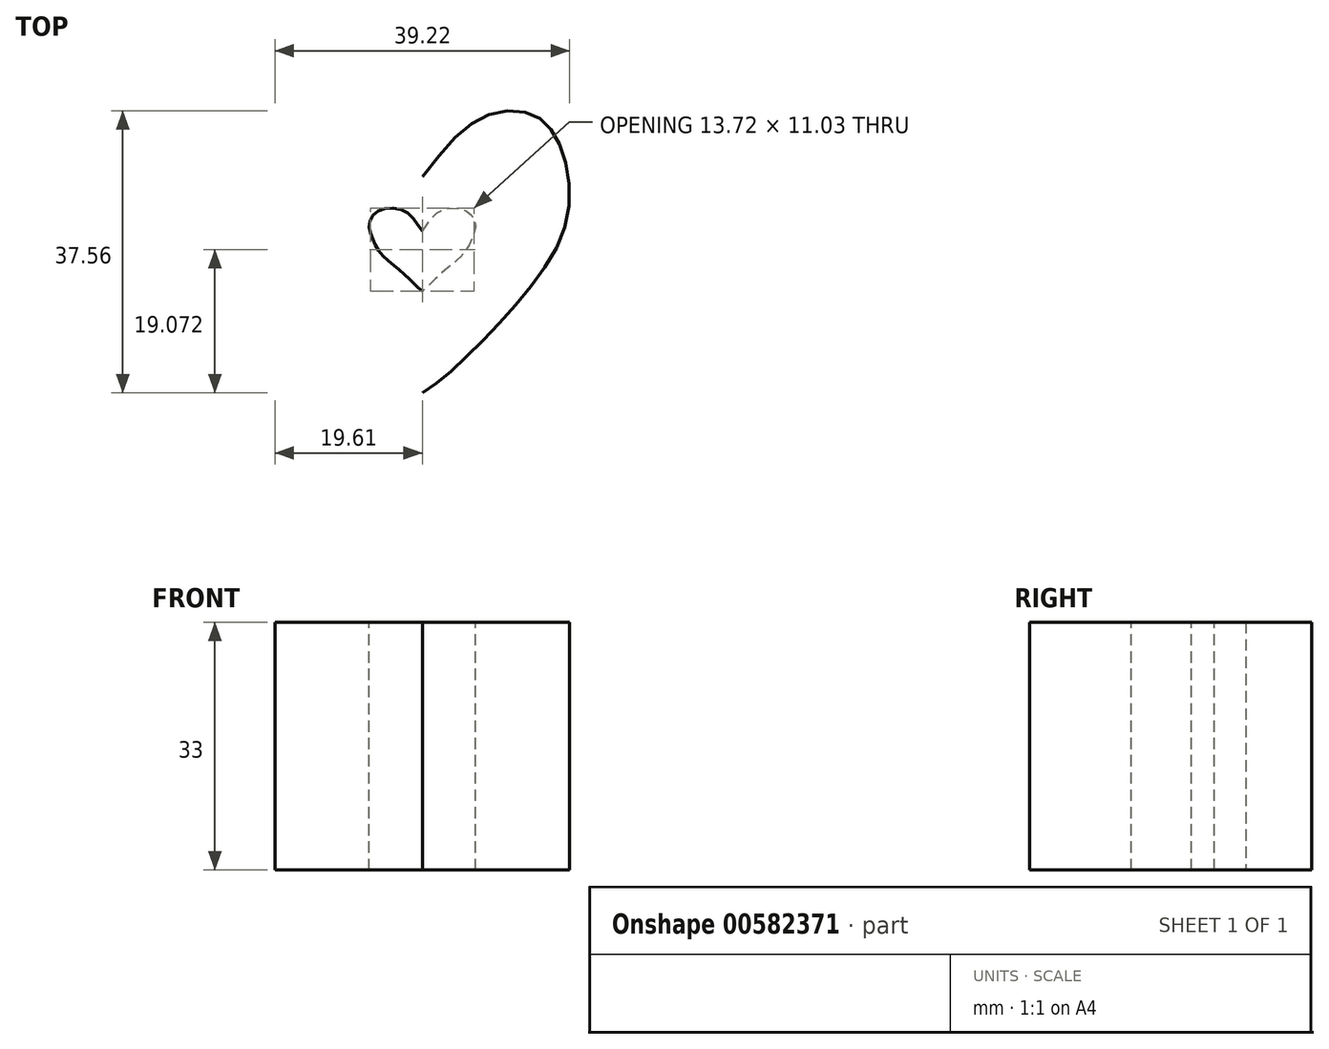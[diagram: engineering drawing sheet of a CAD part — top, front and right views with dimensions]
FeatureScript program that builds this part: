
annotation { "Feature Type Name" : "Feature", "Feature Type Description" : "" }
export const myFeature = defineFeature(function(context is Context, id is Id, definition is map)
    precondition{}
    {
        {
            var Q0;
            Q0=qCreatedBy(makeId("Top.planeOp"),FACE);
            var sketch = newSketch(context, id + "F0", { "sketchPlane" : qUnion([Q0])});
            skFitSpline(sketch, "E0", {"points": [v(0, 10.25) * mm, v(8.19, 18.25) * mm, v(14.83, 18.44) * mm, v(18.35, 14.34) * mm, v(19.36, 5.03) * mm, v(14.25, -4.59) * mm, v(6.05, -13.56) * mm, v(0, -18.53) * mm], "startDerivative": vector(53.63, 68.38) * mm, "endDerivative": vector(-42.6, -24.21) * mm});
            skLineSegment(sketch, "E1", {"start": v(0, 10.25) * mm, "end": v(0, -9.36) * mm, "construction": true});
            skFitSpline(sketch, "E2.MirrorCS", {"points": [v(0, 10.25) * mm, v(-8.19, 18.25) * mm, v(-14.83, 18.44) * mm, v(-18.35, 14.34) * mm, v(-19.36, 5.03) * mm, v(-14.25, -4.59) * mm, v(-6.05, -13.56) * mm, v(0, -18.53) * mm], "startDerivative": vector(-53.63, 68.38) * mm, "endDerivative": vector(42.6, -24.21) * mm});
            skSolve(sketch);
        }
        {
            var Q0;
            {var subQ1=sQuery(id+"F0.wireOp",EDGE,"E0");var subQ3=sQuery(id+"F0.wireOp",EDGE,"rDdCRVCM-XOSB-dXGY-6ydD-Vg9bKhy9GweG");var subQ6=makeQuery(id+"F0.imprint","INTERSECT",VERTEX,{"disambiguationData":[OD(0.0)],"derivedFrom":[subQ3,subQ1]});Q0=makeQuery(id+"F0.imprint","IMPRINT",FACE,{"disambiguationData":[TD([[makeQuery(id+"F0.imprint","IMPRINT",EDGE,{"disambiguationData":[TD([[subQ6,1.0]])],"derivedFrom":subQ3}),1.0]])]});}
            var Q1;
            {var subQ0=sQuery(id+"F0.wireOp",EDGE,"E2.MirrorCS");var subQ1=sQuery(id+"F0.wireOp",EDGE,"rDdCRVCM-XOSB-dXGY-6ydD-Vg9bKhy9GweG");var subQ2=makeQuery(id+"F0.imprint","INTERSECT",VERTEX,{"disambiguationData":[OD(0.0)],"derivedFrom":[subQ1,subQ0]});Q1=makeQuery(id+"F0.imprint","IMPRINT",FACE,{"disambiguationData":[TD([[makeQuery(id+"F0.imprint","IMPRINT",EDGE,{"disambiguationData":[TD([[subQ2,-1.0]])],"derivedFrom":subQ1}),-1.0]])]});}
            var Q2;
            {var subQ0=sQuery(id+"F0.wireOp",EDGE,"E0");var subQ1=sQuery(id+"F0.wireOp",EDGE,"rDdCRVCM-XOSB-dXGY-6ydD-Vg9bKhy9GweG");var subQ2=makeQuery(id+"F0.imprint","INTERSECT",VERTEX,{"disambiguationData":[OD(0.0)],"derivedFrom":[subQ1,subQ0]});Q2=makeQuery(id+"F0.imprint","IMPRINT",FACE,{"disambiguationData":[TD([[makeQuery(id+"F0.imprint","IMPRINT",EDGE,{"disambiguationData":[TD([[subQ2,1.0]])],"derivedFrom":subQ1}),-1.0]])]});}
            var Q3;
            Q3=makeQuery(id+"F0.imprint","IMPRINT",FACE,{"disambiguationData":[TD([[makeQuery(id+"F0.imprint","IMPRINT",EDGE,{"derivedFrom":sQuery(id+"F0.wireOp",EDGE,"E0")}),-1.0]])]});
            extrude(context, id + "F1", {"entities" : qUnion([Q0, Q1, Q2, Q3]), "depth" : 33 * mm, "offsetDistance" : 25 * mm});
        }
        {
            var Q0;
            Q0=makeQuery(id+"F1.opExtrude","CAP_FACE",FACE,{"disambiguationData":[OSD([sQuery(id+"F0.wireOp",EDGE,"E0"),sQuery(id+"F0.wireOp",EDGE,"E2.MirrorCS")])],"isStart":false});
            var sketch = newSketch(context, id + "F2", { "sketchPlane" : qUnion([Q0])});
            skSolve(sketch);
        }
        {
            var Q0;
            Q0=makeQuery(id+"F2.imprint","IMPRINT",FACE,{"disambiguationData":[TD([[makeQuery(id+"F2.imprint","IMPRINT",EDGE,{"derivedFrom":makeQuery(id+"F1.opExtrude","CAP_EDGE",EDGE,{"disambiguationData":[OSD([sQuery(id+"F0.wireOp",EDGE,"E0")])],"isStart":false})}),-1.0]])]});
            var sketch = newSketch(context, id + "F3", { "sketchPlane" : qUnion([Q0])});
            skFitSpline(sketch, "E3", {"points": [v(0, 3.03) * mm, v(2.15, 5.57) * mm, v(5.46, 5.86) * mm, v(7.03, 4.2) * mm, v(6.64, 2.05) * mm, v(5.46, 0) * mm, v(3.32, -1.95) * mm, v(1.37, -3.7) * mm, v(0, -4.97) * mm], "startDerivative": vector(13.38, 17.29) * mm, "endDerivative": vector(-11.6, -7.37) * mm});
            skFitSpline(sketch, "E4.MirrorCS", {"points": [v(0, 3.03) * mm, v(-2.15, 5.57) * mm, v(-5.46, 5.86) * mm, v(-7.03, 4.2) * mm, v(-6.64, 2.05) * mm, v(-5.46, 0) * mm, v(-3.32, -1.95) * mm, v(-1.37, -3.7) * mm, v(0, -4.97) * mm], "startDerivative": vector(-13.38, 17.29) * mm, "endDerivative": vector(11.6, -7.37) * mm});
            skSolve(sketch);
        }
        {
            var Q0;
            Q0=qSketchRegion(id+"F3",true);
            extrude(context, id + "F4", {"entities" : qUnion([Q0]), "operationType" : NewBodyOperationType.REMOVE, "oppositeDirection" : true, "depth" : 76.9 * mm, "offsetDistance" : 25 * mm});
        }
    });
